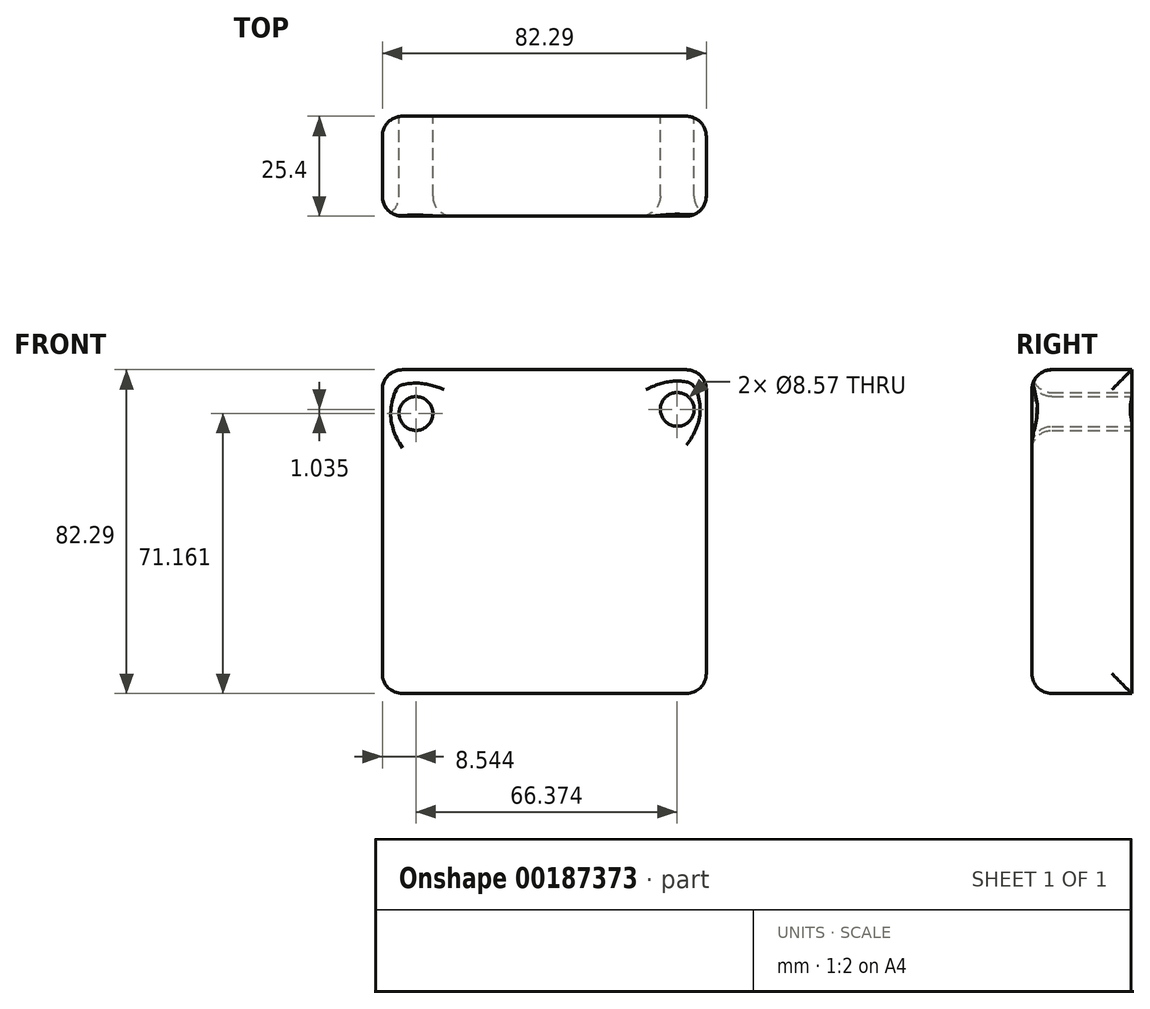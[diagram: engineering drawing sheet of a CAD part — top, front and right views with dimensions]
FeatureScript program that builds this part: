
annotation { "Feature Type Name" : "Feature", "Feature Type Description" : "" }
export const myFeature = defineFeature(function(context is Context, id is Id, definition is map)
    precondition{}
    {
        {
            var Q0;
            Q0=qCreatedBy(makeId("Front.planeOp"),FACE);
            var sketch = newSketch(context, id + "F0", { "sketchPlane" : qUnion([Q0])});
            skLineSegment(sketch, "E0.bottom", {"start": v(-38.8, 39.2) * mm, "end": v(43.5, 39.2) * mm});
            skLineSegment(sketch, "E0.top", {"start": v(-38.8, -43.1) * mm, "end": v(43.5, -43.1) * mm});
            skLineSegment(sketch, "E0.left", {"start": v(-38.8, 39.2) * mm, "end": v(-38.8, -43.1) * mm});
            skLineSegment(sketch, "E0.right", {"start": v(43.5, 39.2) * mm, "end": v(43.5, -43.1) * mm});
            skCircle(sketch, "E1", {"center": v(-30.26, 28.07) * mm, "radius": 4.29 * mm});
            skCircle(sketch, "E2", {"center": v(-30.26, 28.07) * mm, "radius": 2.74 * mm});
            skCircle(sketch, "E3", {"center": v(36.12, 29.1) * mm, "radius": 4.29 * mm});
            skCircle(sketch, "E4", {"center": v(36.12, 29.1) * mm, "radius": 2.74 * mm});
            skSolve(sketch);
        }
        {
            var Q0;
            Q0 = qSketchRegion(id + "F0", true);
            extrude(context, id + "F1", {"entities" : qUnion([Q0]), "depth" : 25.4 * mm});
        }
        {
            var Q0;
            Q0=makeQuery(id+"F1.opExtrude","SWEPT_FACE",FACE,{"disambiguationData":[OSD([sQuery(id+"F0.wireOp",EDGE,"E0.right")])]});
            var Q1;
            Q1=makeQuery(id+"F1.opExtrude","CAP_EDGE",EDGE,{"disambiguationData":[OSD([sQuery(id+"F0.wireOp",EDGE,"E0.bottom")])],"isStart":false});
            var Q2;
            Q2=makeQuery(id+"F1.opExtrude","SWEPT_FACE",FACE,{"disambiguationData":[OSD([sQuery(id+"F0.wireOp",EDGE,"E0.left")])]});
            var Q3;
            Q3=makeQuery(id+"F1.opExtrude","CAP_FACE",FACE,{"disambiguationData":[OSD([sQuery(id+"F0.wireOp",EDGE,"E0.bottom"),sQuery(id+"F0.wireOp",EDGE,"E0.top"),sQuery(id+"F0.wireOp",EDGE,"E0.left"),sQuery(id+"F0.wireOp",EDGE,"E0.right"),sQuery(id+"F0.wireOp",EDGE,"E1"),sQuery(id+"F0.wireOp",EDGE,"E3")])],"isStart":false});
            fillet(context, id + "F2", {"entities" : qUnion([Q0, Q1, Q2, Q3]), "radius" : 5.08 * mm, "tangentPropagation" : true, "allowEdgeOverflow" : false});
        }
        {
            var Q0;
            Q0=makeQuery(id+"F1.opExtrude","CAP_FACE",FACE,{"disambiguationData":[OSD([sQuery(id+"F0.wireOp",EDGE,"E0.bottom"),sQuery(id+"F0.wireOp",EDGE,"E0.top"),sQuery(id+"F0.wireOp",EDGE,"E0.left"),sQuery(id+"F0.wireOp",EDGE,"E0.right"),sQuery(id+"F0.wireOp",EDGE,"E1"),sQuery(id+"F0.wireOp",EDGE,"E3")])],"isStart":false});
            var sketch = newSketch(context, id + "F3", { "sketchPlane" : qUnion([Q0])});
            skLineSegment(sketch, "E5.bottom", {"start": v(28.83, -16.13) * mm, "end": v(-28.83, -16.13) * mm});
            skLineSegment(sketch, "E5.top", {"start": v(28.83, 16.13) * mm, "end": v(-28.83, 16.13) * mm});
            skLineSegment(sketch, "E5.left", {"start": v(28.83, -16.13) * mm, "end": v(28.83, 16.13) * mm});
            skLineSegment(sketch, "E5.right", {"start": v(-28.83, -16.13) * mm, "end": v(-28.83, 16.13) * mm});
            skPoint(sketch, "E5.middle", {"position": v(0, 0) * mm});
            skSolve(sketch);
        }
        {
            var Q0;
            Q0=sQuery(id+"F3.wireOp",EDGE,"E5.top");
            var Q1;
            Q1=sQuery(id+"F3.wireOp",EDGE,"E5.right");
            var Q2;
            Q2=sQuery(id+"F3.wireOp",EDGE,"E5.bottom");
            var Q3;
            Q3=sQuery(id+"F3.wireOp",EDGE,"E5.left");
            extrude(context, id + "F4", {"bodyType" : ToolBodyType.SURFACE, "surfaceEntities" : qUnion([Q0, Q1, Q2, Q3]), "depth" : 25.4 * mm});
        }
        {
            var Q0;
            Q0=makeQuery(id+"F4.opExtrude","SWEPT_FACE",FACE,{"disambiguationData":[OSD([sQuery(id+"F3.wireOp",EDGE,"E5.right")])]});
            var Q1;
            Q1=makeQuery(id+"F4.opExtrude","SWEPT_FACE",FACE,{"disambiguationData":[OSD([sQuery(id+"F3.wireOp",EDGE,"E5.bottom")])]});
            var Q2;
            Q2=makeQuery(id+"F4.opExtrude","SWEPT_FACE",FACE,{"disambiguationData":[OSD([sQuery(id+"F3.wireOp",EDGE,"E5.left")])]});
            fillet(context, id + "F5", {"entities" : qUnion([Q0, Q1, Q2]), "radius" : 5.08 * mm, "tangentPropagation" : true, "allowEdgeOverflow" : false});
        }
    });
